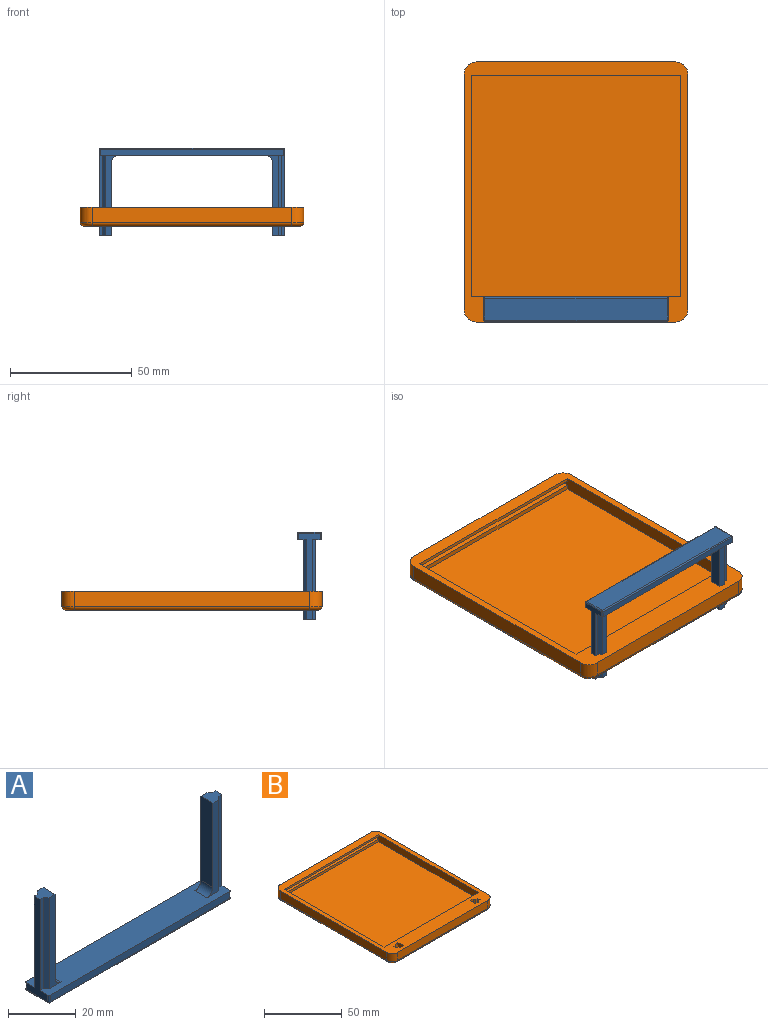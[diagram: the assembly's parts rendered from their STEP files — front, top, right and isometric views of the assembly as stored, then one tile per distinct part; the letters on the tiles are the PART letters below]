
ASSEMBLY  parts=2 mates=1
PART A: 36 faces, bbox 76x10x36 mm
  f0: plane 35.5x9mm, normal (1,0,0), area 105mm2, adj f4,f18,f19,f21,f27,f31,f33
  f1: plane 75x2.5mm, normal (0,1,0), area 187.5mm2, adj f4,f24,f30,f33
  f2: plane 35.5x9mm, normal (-1,0,0), area 105mm2, adj f4,f6,f12,f13,f22,f24,f25
  f3: plane 75x2.5mm, normal (0,-1,0), area 187.5mm2, adj f4,f22,f26,f27
  f4: plane 76x10mm, normal (0,0,1), area 694.2mm2, adj f0,f1,f2,f3,f6,f7,f8,f10
  f5: plane 75x9mm, normal (0,0,-1), area 675mm2, adj f25,f26,f30,f31
  f6: plane 33x1.25mm, normal (0,-1,0), area 41.3mm2, adj f2,f4,f7,f13
  f7: plane 33x1.25mm, normal (-0.71,-0.71,0), area 58.3mm2, adj f4,f6,f8,f13
  f8: plane 33x5mm, normal (0,-1,0), area 83.8mm2, adj f4,f7,f9,f13,f34
  f9: plane 30.5x5mm, normal (1,0,0), area 152.5mm2, adj f8,f10,f13,f34
  f10: plane 33x5mm, normal (0,1,0), area 83.8mm2, adj f4,f9,f11,f13,f34
  f11: plane 33x1.25mm, normal (-0.71,0.71,0), area 58.3mm2, adj f4,f10,f12,f13
  f12: plane 33x1.25mm, normal (0,1,0), area 41.3mm2, adj f2,f4,f11,f13
  f13: plane 5x5mm, normal (0,0,1), area 20.3mm2, adj f2,f6,f7,f8,f9,f10,f11,f12
  f14: plane 33x5mm, normal (0,1,0), area 83.8mm2, adj f4,f15,f20,f21,f35
  f15: plane 30.5x5mm, normal (-1,0,0), area 152.5mm2, adj f14,f16,f21,f35
  f16: plane 33x5mm, normal (0,-1,0), area 83.8mm2, adj f4,f15,f17,f21,f35
  f17: plane 33x1.25mm, normal (0.71,-0.71,0), area 58.3mm2, adj f4,f16,f18,f21
  f18: plane 33x1.25mm, normal (0,-1,0), area 41.3mm2, adj f0,f4,f17,f21
  f19: plane 33x1.25mm, normal (0,1,0), area 41.3mm2, adj f0,f4,f20,f21
  f20: plane 33x1.25mm, normal (0.71,0.71,0), area 58.3mm2, adj f4,f14,f19,f21
  f21: plane 5x5mm, normal (0,0,1), area 20.3mm2, adj f0,f14,f15,f16,f17,f18,f19,f20
  f22: cylinder r=0.5mm len=2.5mm, axis (0,0,1), area 2mm2, adj f2,f3,f4,f23
  f23: sphere r=0.5mm, area 0.4mm2, adj f22,f25,f26
  f24: cylinder r=0.5mm len=2.5mm, axis (0,0,-1), area 2mm2, adj f1,f2,f4,f28
  f25: cylinder r=0.5mm len=9mm, axis (0,-1,0), area 7.1mm2, adj f2,f5,f23,f28
  f26: cylinder r=0.5mm len=75mm, axis (1,0,0), area 58.9mm2, adj f3,f5,f23,f29
  f27: cylinder r=0.5mm len=2.5mm, axis (0,0,-1), area 2mm2, adj f0,f3,f4,f29
  f28: sphere r=0.5mm, area 0.4mm2, adj f24,f25,f30
  f29: sphere r=0.5mm, area 0.4mm2, adj f26,f27,f31
  f30: cylinder r=0.5mm len=75mm, axis (-1,0,0), area 58.9mm2, adj f1,f5,f28,f32
  f31: cylinder r=0.5mm len=9mm, axis (0,1,0), area 7.1mm2, adj f0,f5,f29,f32
  f32: sphere r=0.5mm, area 0.4mm2, adj f30,f31,f33
  f33: cylinder r=0.5mm len=2.5mm, axis (0,0,1), area 2mm2, adj f0,f1,f4,f32
  f34: cylinder r=2.5mm len=5mm, axis (0,1,0), area 19.6mm2, adj f4,f8,f9,f10
  f35: cylinder r=2.5mm len=5mm, axis (0,-1,0), area 19.6mm2, adj f4,f14,f15,f16
PART B: 43 faces, bbox 92.8x107.8x7.8 mm
  f0: plane 104x89mm, normal (0,0,-1), area 9204.9mm2, adj f15,f16,f17,f18,f19,f20,f21,f22
  f1: plane 107x92mm, normal (0,0,1), area 1955.9mm2, adj f3,f4,f5,f6,f7,f8,f9,f12
  f2: plane 86x2mm, normal (0,-1,0), area 172mm2, adj f3,f9,f11,f13
  f3: plane 93.5x5.3mm, normal (-1,0,0), area 487.3mm2, adj f1,f2,f8,f10,f11,f12,f13,f14
  f4: plane 97x6.3mm, normal (1,0,0), area 611.1mm2, adj f1,f31,f34,f42
  f5: plane 82x6.3mm, normal (0,1,0), area 516.6mm2, adj f1,f31,f32,f38
  f6: plane 97x6.3mm, normal (-1,0,0), area 611.1mm2, adj f1,f32,f33,f35
  f7: plane 82x6.3mm, normal (0,-1,0), area 516.6mm2, adj f1,f33,f34,f39
  f8: plane 86x5.3mm, normal (0,1,0), area 455.8mm2, adj f1,f3,f9,f10
  f9: plane 93.5x5.3mm, normal (1,0,0), area 487.3mm2, adj f1,f2,f8,f10,f11,f12,f13,f14
  f10: plane 91x86mm, normal (0,0,1), area 7826mm2, adj f3,f8,f9,f14
  f11: plane 86x2.5mm, normal (0,0,-1), area 215mm2, adj f2,f3,f9,f12
  f12: plane 86x1.4mm, normal (0,-1,0), area 120.4mm2, adj f1,f3,f9,f11
  f13: plane 86x2.5mm, normal (0,0,1), area 215mm2, adj f2,f3,f9,f14
  f14: plane 86x1.9mm, normal (0,-1,0), area 163.4mm2, adj f3,f9,f10,f13
  f15: plane 7.8x2.5mm, normal (0,1,0), area 19.5mm2, adj f0,f1,f16,f22
  f16: plane 7.8x5mm, normal (-1,0,0), area 39mm2, adj f0,f1,f15,f17
  f17: plane 7.8x2.5mm, normal (0,-1,0), area 19.5mm2, adj f0,f1,f16,f18
  f18: plane 7.8x1.25mm, normal (0.71,-0.71,0), area 13.8mm2, adj f0,f1,f17,f19
  f19: plane 7.8x1.25mm, normal (0,-1,0), area 9.8mm2, adj f0,f1,f18,f20
  f20: plane 7.8x2.5mm, normal (1,0,0), area 19.5mm2, adj f0,f1,f19,f21
  f21: plane 7.8x1.25mm, normal (0,1,0), area 9.8mm2, adj f0,f1,f20,f22
  f22: plane 7.8x1.25mm, normal (0.71,0.71,0), area 13.8mm2, adj f0,f1,f15,f21
  f23: plane 7.8x1.25mm, normal (0,1,0), area 9.8mm2, adj f0,f1,f24,f30
  f24: plane 7.8x2.5mm, normal (-1,0,0), area 19.5mm2, adj f0,f1,f23,f25
  f25: plane 7.8x1.25mm, normal (0,-1,0), area 9.8mm2, adj f0,f1,f24,f26
  f26: plane 7.8x1.25mm, normal (-0.71,-0.71,0), area 13.8mm2, adj f0,f1,f25,f27
  f27: plane 7.8x2.5mm, normal (0,-1,0), area 19.5mm2, adj f0,f1,f26,f28
  f28: plane 7.8x5mm, normal (1,0,0), area 39mm2, adj f0,f1,f27,f29
  f29: plane 7.8x2.5mm, normal (0,1,0), area 19.5mm2, adj f0,f1,f28,f30
  f30: plane 7.8x1.25mm, normal (-0.71,0.71,0), area 13.8mm2, adj f0,f1,f23,f29
  f31: cylinder r=5mm len=6.3mm, axis (0,0,1), area 49.5mm2, adj f1,f4,f5,f40
  f32: cylinder r=5mm len=6.3mm, axis (0,0,-1), area 49.5mm2, adj f1,f5,f6,f36
  f33: cylinder r=5mm len=6.3mm, axis (0,0,-1), area 49.5mm2, adj f1,f6,f7,f37
  f34: cylinder r=5mm len=6.3mm, axis (0,0,1), area 49.5mm2, adj f1,f4,f7,f41
  f35: cylinder r=1.5mm len=97mm, axis (0,-1,0), area 228.6mm2, adj f0,f6,f36,f37
  f36: torus R=3.5mm, axis (0,0,1), area 16.5mm2, adj f0,f32,f35,f38
  f37: torus R=3.5mm, axis (0,0,1), area 16.5mm2, adj f0,f33,f35,f39
  f38: cylinder r=1.5mm len=82mm, axis (-1,0,0), area 193.2mm2, adj f0,f5,f36,f40
  f39: cylinder r=1.5mm len=82mm, axis (1,0,0), area 193.2mm2, adj f0,f7,f37,f41
  f40: torus R=3.5mm, axis (0,0,1), area 16.5mm2, adj f0,f31,f38,f42
  f41: torus R=3.5mm, axis (0,0,1), area 16.5mm2, adj f0,f34,f39,f42
  f42: cylinder r=1.5mm len=97mm, axis (0,1,0), area 228.6mm2, adj f0,f4,f40,f41
PLACE A rot(axis=(0,-1,0),180deg) t=(-16.32,-50.74,31.22)mm
PLACE B t=(-16.32,1.26,0.02)mm
MATE slider A.f21 <-> B.f0  axis (0,0,-1) through (-49.32,-48.24,-4.78)mm
